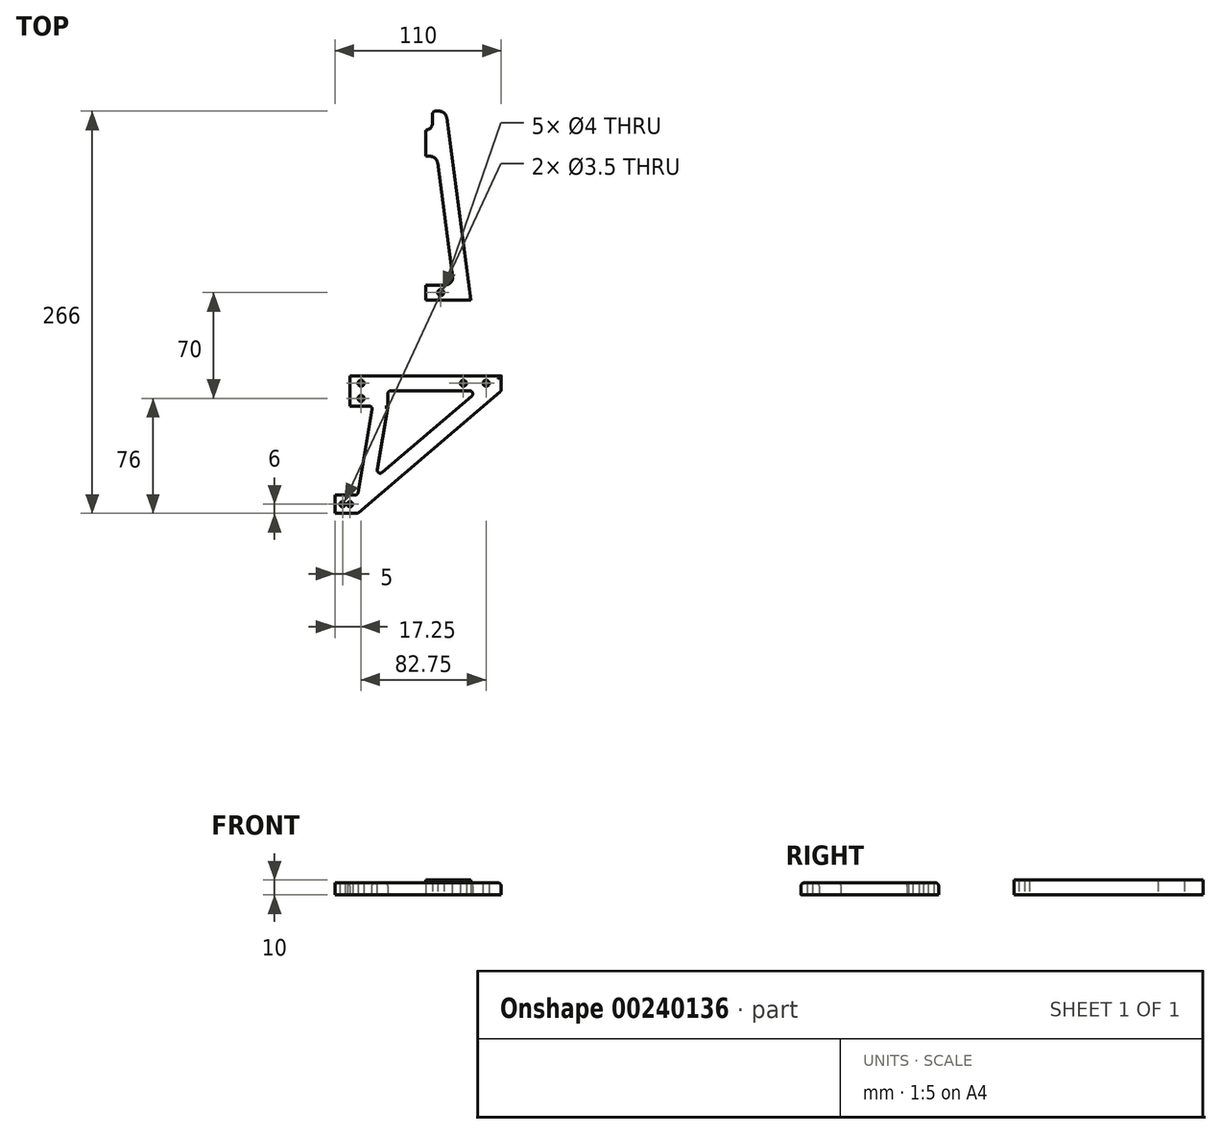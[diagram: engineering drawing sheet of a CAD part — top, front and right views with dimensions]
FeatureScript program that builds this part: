
annotation { "Feature Type Name" : "Feature", "Feature Type Description" : "" }
export const myFeature = defineFeature(function(context is Context, id is Id, definition is map)
    precondition{}
    {
        {
            var Q0;
            Q0=qCreatedBy(makeId("Top.planeOp"),FACE);
            var sketch = newSketch(context, id + "F0", { "sketchPlane" : qUnion([Q0])});
            skLineSegment(sketch, "E0.top", {"start": v(0, 75) * mm, "end": v(-30, 75) * mm});
            skPoint(sketch, "E0.middle", {"position": v(0, 0) * mm});
            skLineSegment(sketch, "E1", {"start": v(-30, 75) * mm, "end": v(-50, -75) * mm});
            skPoint(sketch, "E0.right.end.orphan", {"position": v(-50, 75) * mm});
            skPoint(sketch, "E0.left.end.orphan", {"position": v(50, 75) * mm});
            skLineSegment(sketch, "E2", {"start": v(0, 0) * mm, "end": v(0, 6) * mm});
            skLineSegment(sketch, "E3", {"start": v(-50, -75) * mm, "end": v(-40, -75) * mm});
            skLineSegment(sketch, "E4", {"start": v(-30, 75) * mm, "end": v(-20, 75) * mm});
            skLineSegment(sketch, "E5", {"start": v(0, 75) * mm, "end": v(0, 65) * mm});
            skLineSegment(sketch, "E6", {"start": v(0, 65) * mm, "end": v(-21.33, 65) * mm});
            skLineSegment(sketch, "E7", {"start": v(0, -75) * mm, "end": v(0, -65) * mm});
            skLineSegment(sketch, "E8", {"start": v(0, -65) * mm, "end": v(-38.67, -65) * mm});
            skLineSegment(sketch, "E9", {"start": v(0, 6) * mm, "end": v(-29.2, 6) * mm});
            skLineSegment(sketch, "E10", {"start": v(0, 0) * mm, "end": v(0, -6) * mm});
            skLineSegment(sketch, "E11", {"start": v(0, -6) * mm, "end": v(-30.8, -6) * mm});
            skLineSegment(sketch, "E12.trimOffspring", {"start": v(-30.8, -6) * mm, "end": v(-38.67, -65) * mm});
            skLineSegment(sketch, "E13", {"start": v(-21.33, 65) * mm, "end": v(-29.2, 6) * mm});
            skLineSegment(sketch, "E14.trimOffspring", {"start": v(0, -75) * mm, "end": v(-50, -75) * mm});
            skPoint(sketch, "E0.bottom.start.orphan", {"position": v(50, -75) * mm});
            skCircle(sketch, "E15", {"center": v(-15, 0) * mm, "radius": 2 * mm});
            skLineSegment(sketch, "E16", {"start": v(0, 65) * mm, "end": v(0, 70) * mm});
            skCircle(sketch, "E17", {"center": v(-10.41, 70) * mm, "radius": 2 * mm});
            skSolve(sketch);
        }
        {
            var Q0;
            Q0=qSketchRegion(id+"F0",true);
            extrude(context, id + "F1", {"entities" : qUnion([Q0]), "depth" : 10 * mm});
        }
        {
            var Q0;
            Q0=makeQuery(id+"F1.opExtrude","SWEPT_EDGE",EDGE,{"disambiguationData":[OSD([sQuery(id+"F0.wireOp",EDGE,"E6"),sQuery(id+"F0.wireOp",EDGE,"E13")])]});
            var Q1;
            Q1=makeQuery(id+"F1.opExtrude","SWEPT_EDGE",EDGE,{"disambiguationData":[OSD([sQuery(id+"F0.wireOp",EDGE,"E11"),sQuery(id+"F0.wireOp",EDGE,"E12.trimOffspring")])]});
            var Q2;
            Q2=makeQuery(id+"F1.opExtrude","SWEPT_EDGE",EDGE,{"disambiguationData":[OSD([sQuery(id+"F0.wireOp",EDGE,"E9"),sQuery(id+"F0.wireOp",EDGE,"E13")])]});
            var Q3;
            Q3=makeQuery(id+"F1.opExtrude","SWEPT_EDGE",EDGE,{"disambiguationData":[OSD([sQuery(id+"F0.wireOp",EDGE,"E8"),sQuery(id+"F0.wireOp",EDGE,"E12.trimOffspring")])]});
            var Q4;
            Q4=makeQuery(id+"F1.opExtrude","SWEPT_EDGE",EDGE,{"disambiguationData":[OSD([sQuery(id+"F0.wireOp",EDGE,"E1"),sQuery(id+"F0.wireOp",EDGE,"E14.trimOffspring")])]});
            fillet(context, id + "F2", {"entities" : qUnion([Q0, Q1, Q2, Q3, Q4]), "radius" : 5 * mm, "tangentPropagation" : true, "allowEdgeOverflow" : false});
        }
        {
            var Q0;
            Q0=makeQuery(id+"F1.opExtrude","SWEPT_BODY",BODY,{"disambiguationData":[OSD([sQuery(id+"F0.wireOp",EDGE,"E0.top"),sQuery(id+"F0.wireOp",EDGE,"E1"),sQuery(id+"F0.wireOp",EDGE,"E2"),sQuery(id+"F0.wireOp",EDGE,"E4"),sQuery(id+"F0.wireOp",EDGE,"E5"),sQuery(id+"F0.wireOp",EDGE,"E6"),sQuery(id+"F0.wireOp",EDGE,"E7"),sQuery(id+"F0.wireOp",EDGE,"E8"),sQuery(id+"F0.wireOp",EDGE,"E9"),sQuery(id+"F0.wireOp",EDGE,"E10"),sQuery(id+"F0.wireOp",EDGE,"E11"),sQuery(id+"F0.wireOp",EDGE,"E12.trimOffspring"),sQuery(id+"F0.wireOp",EDGE,"E13"),sQuery(id+"F0.wireOp",EDGE,"E14.trimOffspring"),sQuery(id+"F0.wireOp",EDGE,"E15"),sQuery(id+"F0.wireOp",EDGE,"E16"),sQuery(id+"F0.wireOp",EDGE,"E17")])]});
            var Q1;
            Q1=qCreatedBy(makeId("Right.planeOp"),FACE);
            mirror(context, id + "F3", {"operationType" : NewBodyOperationType.ADD, "entities" : qUnion([Q0]), "mirrorPlane" : qUnion([Q1])});
        }
        {
            var Q0;
            Q0=qCreatedBy(makeId("Top.planeOp"),FACE);
            var sketch = newSketch(context, id + "F4", { "sketchPlane" : qUnion([Q0])});
            skLineSegment(sketch, "E18", {"start": v(0, 0) * mm, "end": v(40, 0) * mm});
            skLineSegment(sketch, "E19", {"start": v(0, 75) * mm, "end": v(30, 75) * mm});
            skLineSegment(sketch, "E20", {"start": v(0, 75) * mm, "end": v(0, 85) * mm});
            skLineSegment(sketch, "E21", {"start": v(4.5, 200) * mm, "end": v(13.33, 200) * mm});
            skLineSegment(sketch, "E22", {"start": v(30, 75) * mm, "end": v(13.33, 200) * mm});
            skArc(sketch, "E23", {"start": v(0, 187.5) * mm, "mid": v(3.18, 188.82) * mm, "end": v(4.5, 192) * mm});
            skLineSegment(sketch, "E24", {"start": v(4.5, 200) * mm, "end": v(4.5, 192) * mm});
            skLineSegment(sketch, "E25", {"start": v(0, 75) * mm, "end": v(0, 80) * mm});
            skCircle(sketch, "E26", {"center": v(10, 80) * mm, "radius": 2 * mm});
            skLineSegment(sketch, "E27", {"start": v(0, 75) * mm, "end": v(10, 75) * mm});
            skLineSegment(sketch, "E28", {"start": v(10, 85) * mm, "end": v(18.67, 85) * mm});
            skLineSegment(sketch, "E29", {"start": v(18.67, 85) * mm, "end": v(10, 150) * mm});
            skLineSegment(sketch, "E30", {"start": v(10, 85) * mm, "end": v(0, 85) * mm});
            skLineSegment(sketch, "E31", {"start": v(18.67, 85) * mm, "end": v(7.31, 170.17) * mm});
            skLineSegment(sketch, "E32", {"start": v(7.31, 170.17) * mm, "end": v(0, 170.17) * mm});
            skLineSegment(sketch, "E33.trimOffspring", {"start": v(0, 170.17) * mm, "end": v(0, 187.5) * mm});
            skSolve(sketch);
        }
        {
            var Q0;
            Q0=qSketchRegion(id+"F4",true);
            extrude(context, id + "F5", {"entities" : qUnion([Q0]), "depth" : 10 * mm});
        }
        {
            var Q0;
            Q0=makeQuery(id+"F5.opExtrude","SWEPT_BODY",BODY,{"disambiguationData":[OSD([sQuery(id+"F4.wireOp",EDGE,"E19"),sQuery(id+"F4.wireOp",EDGE,"E20"),sQuery(id+"F4.wireOp",EDGE,"E21"),sQuery(id+"F4.wireOp",EDGE,"E22"),sQuery(id+"F4.wireOp",EDGE,"E23"),sQuery(id+"F4.wireOp",EDGE,"E24"),sQuery(id+"F4.wireOp",EDGE,"E25"),sQuery(id+"F4.wireOp",EDGE,"E26"),sQuery(id+"F4.wireOp",EDGE,"E27"),sQuery(id+"F4.wireOp",EDGE,"E28"),sQuery(id+"F4.wireOp",EDGE,"E30"),sQuery(id+"F4.wireOp",EDGE,"E31"),sQuery(id+"F4.wireOp",EDGE,"E32"),sQuery(id+"F4.wireOp",EDGE,"E33.trimOffspring")])]});
            var Q1;
            Q1=qCreatedBy(makeId("Right.planeOp"),FACE);
            mirror(context, id + "F6", {"entities" : qUnion([Q0]), "mirrorPlane" : qUnion([Q1])});
        }
        {
            var Q0;
            Q0=makeQuery(id+"F6.opPattern","COPY",EDGE,{"derivedFrom":makeQuery(id+"F5.opExtrude","SWEPT_EDGE",EDGE,{"disambiguationData":[OSD([sQuery(id+"F4.wireOp",EDGE,"E31"),sQuery(id+"F4.wireOp",EDGE,"E32")])]}),"instanceName":"1"});
            var Q1;
            Q1=makeQuery(id+"F5.opExtrude","SWEPT_EDGE",EDGE,{"disambiguationData":[OSD([sQuery(id+"F4.wireOp",EDGE,"E31"),sQuery(id+"F4.wireOp",EDGE,"E32")])]});
            var Q2;
            Q2=makeQuery(id+"F6.opPattern","COPY",EDGE,{"derivedFrom":makeQuery(id+"F5.opExtrude","SWEPT_EDGE",EDGE,{"disambiguationData":[OSD([sQuery(id+"F4.wireOp",EDGE,"E28"),sQuery(id+"F4.wireOp",EDGE,"E31")])]}),"instanceName":"1"});
            var Q3;
            Q3=makeQuery(id+"F5.opExtrude","SWEPT_EDGE",EDGE,{"disambiguationData":[OSD([sQuery(id+"F4.wireOp",EDGE,"E28"),sQuery(id+"F4.wireOp",EDGE,"E31")])]});
            var Q4;
            Q4=makeQuery(id+"F6.opPattern","COPY",EDGE,{"derivedFrom":makeQuery(id+"F5.opExtrude","SWEPT_EDGE",EDGE,{"disambiguationData":[OSD([sQuery(id+"F4.wireOp",EDGE,"E21"),sQuery(id+"F4.wireOp",EDGE,"E22")])]}),"instanceName":"1"});
            var Q5;
            Q5=makeQuery(id+"F5.opExtrude","SWEPT_EDGE",EDGE,{"disambiguationData":[OSD([sQuery(id+"F4.wireOp",EDGE,"E21"),sQuery(id+"F4.wireOp",EDGE,"E22")])]});
            fillet(context, id + "F7", {"entities" : qUnion([Q0, Q1, Q2, Q3, Q4, Q5]), "radius" : 5 * mm, "tangentPropagation" : true, "allowEdgeOverflow" : false});
        }
        {
            var Q0;
            Q0=makeQuery(id+"F5.opExtrude","SWEPT_EDGE",EDGE,{"disambiguationData":[OSD([sQuery(id+"F4.wireOp",EDGE,"E21"),sQuery(id+"F4.wireOp",EDGE,"E24")])]});
            var Q1;
            Q1=makeQuery(id+"F6.opPattern","COPY",EDGE,{"derivedFrom":makeQuery(id+"F5.opExtrude","SWEPT_EDGE",EDGE,{"disambiguationData":[OSD([sQuery(id+"F4.wireOp",EDGE,"E21"),sQuery(id+"F4.wireOp",EDGE,"E24")])]}),"instanceName":"1"});
            fillet(context, id + "F8", {"entities" : qUnion([Q0, Q1]), "radius" : 2 * mm, "tangentPropagation" : true, "allowEdgeOverflow" : false});
        }
        {
            var Q0;
            Q0=qCreatedBy(makeId("Top.planeOp"),FACE);
            var sketch = newSketch(context, id + "F9", { "sketchPlane" : qUnion([Q0])});
            skLineSegment(sketch, "E34", {"start": v(0, 0) * mm, "end": v(0, 6) * mm});
            skLineSegment(sketch, "E35", {"start": v(0, 6) * mm, "end": v(-6, 6) * mm});
            skLineSegment(sketch, "E36", {"start": v(-6, 6) * mm, "end": v(-6, -6) * mm});
            skLineSegment(sketch, "E37", {"start": v(-6, -6) * mm, "end": v(0, -6) * mm});
            skLineSegment(sketch, "E38", {"start": v(0, -6) * mm, "end": v(0, 0) * mm});
            skSolve(sketch);
        }
        {
            var Q0;
            Q0=qSketchRegion(id+"F9",true);
            extrude(context, id + "F10", {"entities" : qUnion([Q0]), "operationType" : NewBodyOperationType.ADD, "depth" : 25 * mm});
        }
        {
            var Q0;
            Q0=makeQuery(id+"F10.opExtrude","SWEPT_EDGE",EDGE,{"disambiguationData":[OSD([sQuery(id+"F9.wireOp",EDGE,"E36"),sQuery(id+"F9.wireOp",EDGE,"E37")])]});
            var Q1;
            Q1=makeQuery(id+"F10.opExtrude","CAP_EDGE",EDGE,{"disambiguationData":[OSD([sQuery(id+"F9.wireOp",EDGE,"E36")])],"isStart":false});
            var Q2;
            Q2=makeQuery(id+"F10.opExtrude","CAP_EDGE",EDGE,{"disambiguationData":[OSD([sQuery(id+"F9.wireOp",EDGE,"E37")])],"isStart":false});
            var Q3;
            Q3=makeQuery(id+"F10.opExtrude","SWEPT_EDGE",EDGE,{"disambiguationData":[OSD([sQuery(id+"F9.wireOp",EDGE,"E35"),sQuery(id+"F9.wireOp",EDGE,"E36")])]});
            var Q4;
            Q4=makeQuery(id+"F10.opExtrude","CAP_EDGE",EDGE,{"disambiguationData":[OSD([sQuery(id+"F9.wireOp",EDGE,"E35")])],"isStart":false});
            fillet(context, id + "F11", {"entities" : qUnion([Q0, Q1, Q2, Q3, Q4]), "radius" : 1.5 * mm, "tangentPropagation" : true, "allowEdgeOverflow" : false});
        }
        {
            var Q0;
            Q0=qCreatedBy(makeId("Right.planeOp"),FACE);
            var sketch = newSketch(context, id + "F12", { "sketchPlane" : qUnion([Q0])});
            skCircle(sketch, "E39", {"center": v(0, 20) * mm, "radius": 1.75 * mm});
            skCircle(sketch, "E40", {"center": v(0, 15) * mm, "radius": 1.75 * mm});
            skSolve(sketch);
        }
        {
            var Q0;
            Q0=qSketchRegion(id+"F12",true);
            extrude(context, id + "F13", {"entities" : qUnion([Q0]), "endBound" : BoundingType.SYMMETRIC, "depth" : 25 * mm});
        }
        {
            var Q0;
            Q0=makeQuery(id+"F13.opExtrude","SWEPT_BODY",BODY,{"disambiguationData":[OSD([sQuery(id+"F12.wireOp",EDGE,"E40")])]});
            var Q1;
            Q1=makeQuery(id+"F13.opExtrude","SWEPT_BODY",BODY,{"disambiguationData":[OSD([sQuery(id+"F12.wireOp",EDGE,"E39")])]});
            var Q2;
            Q2=makeQuery(id+"F1.opExtrude","SWEPT_BODY",BODY,{"disambiguationData":[OSD([sQuery(id+"F0.wireOp",EDGE,"E0.top"),sQuery(id+"F0.wireOp",EDGE,"E1"),sQuery(id+"F0.wireOp",EDGE,"E2"),sQuery(id+"F0.wireOp",EDGE,"E4"),sQuery(id+"F0.wireOp",EDGE,"E5"),sQuery(id+"F0.wireOp",EDGE,"E6"),sQuery(id+"F0.wireOp",EDGE,"E7"),sQuery(id+"F0.wireOp",EDGE,"E8"),sQuery(id+"F0.wireOp",EDGE,"E9"),sQuery(id+"F0.wireOp",EDGE,"E10"),sQuery(id+"F0.wireOp",EDGE,"E11"),sQuery(id+"F0.wireOp",EDGE,"E12.trimOffspring"),sQuery(id+"F0.wireOp",EDGE,"E13"),sQuery(id+"F0.wireOp",EDGE,"E14.trimOffspring"),sQuery(id+"F0.wireOp",EDGE,"E15"),sQuery(id+"F0.wireOp",EDGE,"E16"),sQuery(id+"F0.wireOp",EDGE,"E17")])]});
            booleanBodies(context, id + "F14", {"operationType" : BooleanOperationType.SUBTRACTION, "tools" : qUnion([Q0, Q1]), "targets" : qUnion([Q2])});
        }
        {
            var Q0;
            Q0=qCreatedBy(makeId("Top.planeOp"),FACE);
            var sketch = newSketch(context, id + "F15", { "sketchPlane" : qUnion([Q0])});
            skLineSegment(sketch, "E41.bottom", {"start": v(15, 65) * mm, "end": v(-15, 65) * mm});
            skLineSegment(sketch, "E41.top", {"start": v(15, 85) * mm, "end": v(-15, 85) * mm});
            skLineSegment(sketch, "E41.left", {"start": v(15, 65) * mm, "end": v(15, 85) * mm});
            skLineSegment(sketch, "E41.right", {"start": v(-15, 65) * mm, "end": v(-15, 85) * mm});
            skPoint(sketch, "E41.middle", {"position": v(0, 75) * mm});
            skLineSegment(sketch, "E42", {"start": v(0, 75) * mm, "end": v(0, 85) * mm});
            skLineSegment(sketch, "E43", {"start": v(0, 85) * mm, "end": v(0, 65) * mm});
            skLineSegment(sketch, "E44", {"start": v(0, 65) * mm, "end": v(-6, 65) * mm});
            skLineSegment(sketch, "E45", {"start": v(-6, 65) * mm, "end": v(-6, 85) * mm});
            skLineSegment(sketch, "E46", {"start": v(-6, 85) * mm, "end": v(0, 85) * mm});
            skSolve(sketch);
        }
        {
            var Q0;
            Q0=qSketchRegion(id+"F15",true);
            extrude(context, id + "F16", {"entities" : qUnion([Q0]), "depth" : 10 * mm});
        }
        {
            var Q0;
            Q0=qCreatedBy(makeId("Top.planeOp"),FACE);
            var sketch = newSketch(context, id + "F17", { "sketchPlane" : qUnion([Q0])});
            skLineSegment(sketch, "E47", {"start": v(0, 65) * mm, "end": v(0, 85) * mm});
            skLineSegment(sketch, "E48", {"start": v(0, 85) * mm, "end": v(-6, 85) * mm});
            skLineSegment(sketch, "E49", {"start": v(-6, 85) * mm, "end": v(-6, 65) * mm});
            skLineSegment(sketch, "E50", {"start": v(-6, 65) * mm, "end": v(0, 65) * mm});
            skSolve(sketch);
        }
        {
            var Q0;
            Q0=qSketchRegion(id+"F17",true);
            extrude(context, id + "F18", {"entities" : qUnion([Q0]), "depth" : 25 * mm});
        }
        {
            var Q0;
            Q0=makeQuery(id+"F16.opExtrude","SWEPT_BODY",BODY,{"disambiguationData":[OSD([sQuery(id+"F15.wireOp",EDGE,"E41.bottom"),sQuery(id+"F15.wireOp",EDGE,"E41.top"),sQuery(id+"F15.wireOp",EDGE,"E41.left"),sQuery(id+"F15.wireOp",EDGE,"E41.right"),sQuery(id+"F15.wireOp",EDGE,"E44"),sQuery(id+"F15.wireOp",EDGE,"E46")])]});
            var Q1;
            Q1=makeQuery(id+"F18.opExtrude","SWEPT_BODY",BODY,{"disambiguationData":[OSD([sQuery(id+"F17.wireOp",EDGE,"E47"),sQuery(id+"F17.wireOp",EDGE,"E48"),sQuery(id+"F17.wireOp",EDGE,"E49"),sQuery(id+"F17.wireOp",EDGE,"E50")])]});
            booleanBodies(context, id + "F19", {"operationType" : BooleanOperationType.UNION, "tools" : qUnion([Q0, Q1])});
        }
        {
            var Q0;
            Q0=makeQuery(id+"F16.opExtrude","SWEPT_BODY",BODY,{"disambiguationData":[OSD([sQuery(id+"F15.wireOp",EDGE,"E41.bottom"),sQuery(id+"F15.wireOp",EDGE,"E41.top"),sQuery(id+"F15.wireOp",EDGE,"E41.left"),sQuery(id+"F15.wireOp",EDGE,"E41.right"),sQuery(id+"F15.wireOp",EDGE,"E44"),sQuery(id+"F15.wireOp",EDGE,"E46")])]});
            transform(context, id + "F20", {"entities" : qUnion([Q0]), "transformType" : TransformType.TRANSLATION_3D, "dx" : 0 * mm, "dy" : 0 * mm, "dz" : 10 * mm, "makeCopy" : false});
        }
        {
            var Q0;
            Q0=qCreatedBy(makeId("Top.planeOp"),FACE);
            var sketch = newSketch(context, id + "F21", { "sketchPlane" : qUnion([Q0])});
            skCircle(sketch, "E51", {"center": v(-10, 80) * mm, "radius": 2 * mm});
            skCircle(sketch, "E52", {"center": v(10, 80) * mm, "radius": 2 * mm});
            skCircle(sketch, "E53", {"center": v(-10.4, 70) * mm, "radius": 2 * mm});
            skCircle(sketch, "E54", {"center": v(10.4, 70) * mm, "radius": 2 * mm});
            skSolve(sketch);
        }
        {
            var Q0;
            Q0=qSketchRegion(id+"F21",true);
            extrude(context, id + "F22", {"entities" : qUnion([Q0]), "depth" : 30 * mm});
        }
        {
            var Q0;
            Q0=makeQuery(id+"F22.opExtrude","SWEPT_BODY",BODY,{"disambiguationData":[OSD([sQuery(id+"F21.wireOp",EDGE,"E54")])]});
            var Q1;
            Q1=makeQuery(id+"F22.opExtrude","SWEPT_BODY",BODY,{"disambiguationData":[OSD([sQuery(id+"F21.wireOp",EDGE,"E53")])]});
            var Q2;
            Q2=makeQuery(id+"F22.opExtrude","SWEPT_BODY",BODY,{"disambiguationData":[OSD([sQuery(id+"F21.wireOp",EDGE,"E52")])]});
            var Q3;
            Q3=makeQuery(id+"F22.opExtrude","SWEPT_BODY",BODY,{"disambiguationData":[OSD([sQuery(id+"F21.wireOp",EDGE,"E51")])]});
            var Q4;
            Q4=makeQuery(id+"F16.opExtrude","SWEPT_BODY",BODY,{"disambiguationData":[OSD([sQuery(id+"F15.wireOp",EDGE,"E41.bottom"),sQuery(id+"F15.wireOp",EDGE,"E41.top"),sQuery(id+"F15.wireOp",EDGE,"E41.left"),sQuery(id+"F15.wireOp",EDGE,"E41.right"),sQuery(id+"F15.wireOp",EDGE,"E44"),sQuery(id+"F15.wireOp",EDGE,"E46")])]});
            booleanBodies(context, id + "F23", {"operationType" : BooleanOperationType.SUBTRACTION, "tools" : qUnion([Q0, Q1, Q2, Q3]), "targets" : qUnion([Q4])});
        }
        {
            var Q0;
            Q0=qCreatedBy(makeId("Right.planeOp"),FACE);
            var sketch = newSketch(context, id + "F24", { "sketchPlane" : qUnion([Q0])});
            skCircle(sketch, "E55", {"center": v(80, 27.23) * mm, "radius": 2 * mm});
            skCircle(sketch, "E56", {"center": v(70, 27.23) * mm, "radius": 2 * mm});
            skSolve(sketch);
        }
        {
            var Q0;
            Q0=qSketchRegion(id+"F24",true);
            extrude(context, id + "F25", {"entities" : qUnion([Q0]), "endBound" : BoundingType.SYMMETRIC, "depth" : 25 * mm});
        }
        {
            var Q0;
            Q0=makeQuery(id+"F25.opExtrude","SWEPT_BODY",BODY,{"disambiguationData":[OSD([sQuery(id+"F24.wireOp",EDGE,"E56")])]});
            var Q1;
            Q1=makeQuery(id+"F25.opExtrude","SWEPT_BODY",BODY,{"disambiguationData":[OSD([sQuery(id+"F24.wireOp",EDGE,"E55")])]});
            var Q2;
            Q2=makeQuery(id+"F16.opExtrude","SWEPT_BODY",BODY,{"disambiguationData":[OSD([sQuery(id+"F15.wireOp",EDGE,"E41.bottom"),sQuery(id+"F15.wireOp",EDGE,"E41.top"),sQuery(id+"F15.wireOp",EDGE,"E41.left"),sQuery(id+"F15.wireOp",EDGE,"E41.right"),sQuery(id+"F15.wireOp",EDGE,"E44"),sQuery(id+"F15.wireOp",EDGE,"E46")])]});
            booleanBodies(context, id + "F26", {"operationType" : BooleanOperationType.SUBTRACTION, "tools" : qUnion([Q0, Q1]), "targets" : qUnion([Q2])});
        }
        {
            var Q0;
            Q0=makeQuery(id+"F18.opExtrude","SWEPT_EDGE",EDGE,{"disambiguationData":[OSD([sQuery(id+"F17.wireOp",EDGE,"E49"),sQuery(id+"F17.wireOp",EDGE,"E50")])]});
            var Q1;
            Q1=makeQuery(id+"F18.opExtrude","CAP_EDGE",EDGE,{"disambiguationData":[OSD([sQuery(id+"F17.wireOp",EDGE,"E50")])],"isStart":false});
            var Q2;
            {var subQ0=sQuery(id+"F15.wireOp",EDGE,"E44");var subQ1=sQuery(id+"F15.wireOp",EDGE,"E41.bottom");var subQ2=sQuery(id+"F15.wireOp",EDGE,"E41.right");Q2=makeQuery(id+"F19.opBoolean","SPLIT",EDGE,{"disambiguationData":[TD([makeQuery(id+"F16.opExtrude","SWEPT_FACE",FACE,{"disambiguationData":[OSD([subQ2])]})])],"derivedFrom":makeQuery(id+"F16.opExtrude","CAP_EDGE",EDGE,{"disambiguationData":[OSD([subQ1,subQ0])],"isStart":false})});}
            var Q3;
            Q3=makeQuery(id+"F16.opExtrude","SWEPT_EDGE",EDGE,{"disambiguationData":[OSD([sQuery(id+"F15.wireOp",EDGE,"E41.bottom"),sQuery(id+"F15.wireOp",EDGE,"E41.right")])]});
            var Q4;
            {var subQ0=sQuery(id+"F15.wireOp",EDGE,"E41.left");var subQ1=sQuery(id+"F15.wireOp",EDGE,"E44");var subQ2=sQuery(id+"F15.wireOp",EDGE,"E41.bottom");Q4=makeQuery(id+"F19.opBoolean","SPLIT",EDGE,{"disambiguationData":[TD([makeQuery(id+"F16.opExtrude","SWEPT_FACE",FACE,{"disambiguationData":[OSD([subQ0])]})])],"derivedFrom":makeQuery(id+"F16.opExtrude","CAP_EDGE",EDGE,{"disambiguationData":[OSD([subQ2,subQ1])],"isStart":false})});}
            var Q5;
            Q5=makeQuery(id+"F16.opExtrude","SWEPT_EDGE",EDGE,{"disambiguationData":[OSD([sQuery(id+"F15.wireOp",EDGE,"E41.bottom"),sQuery(id+"F15.wireOp",EDGE,"E41.left")])]});
            var Q6;
            Q6=makeQuery(id+"F16.opExtrude","CAP_EDGE",EDGE,{"disambiguationData":[OSD([sQuery(id+"F15.wireOp",EDGE,"E41.left")])],"isStart":false});
            var Q7;
            Q7=makeQuery(id+"F16.opExtrude","CAP_EDGE",EDGE,{"disambiguationData":[OSD([sQuery(id+"F15.wireOp",EDGE,"E41.right")])],"isStart":false});
            var Q8;
            Q8=makeQuery(id+"F18.opExtrude","CAP_EDGE",EDGE,{"disambiguationData":[OSD([sQuery(id+"F17.wireOp",EDGE,"E49")])],"isStart":false});
            var Q9;
            {var subQ0=sQuery(id+"F15.wireOp",EDGE,"E41.right");var subQ1=sQuery(id+"F15.wireOp",EDGE,"E46");var subQ2=sQuery(id+"F15.wireOp",EDGE,"E41.top");Q9=makeQuery(id+"F19.opBoolean","SPLIT",EDGE,{"disambiguationData":[TD([makeQuery(id+"F16.opExtrude","SWEPT_FACE",FACE,{"disambiguationData":[OSD([subQ0])]})])],"derivedFrom":makeQuery(id+"F16.opExtrude","CAP_EDGE",EDGE,{"disambiguationData":[OSD([subQ2,subQ1])],"isStart":false})});}
            var Q10;
            Q10=makeQuery(id+"F16.opExtrude","SWEPT_EDGE",EDGE,{"disambiguationData":[OSD([sQuery(id+"F15.wireOp",EDGE,"E41.top"),sQuery(id+"F15.wireOp",EDGE,"E41.right")])]});
            var Q11;
            Q11=makeQuery(id+"F18.opExtrude","SWEPT_EDGE",EDGE,{"disambiguationData":[OSD([sQuery(id+"F17.wireOp",EDGE,"E48"),sQuery(id+"F17.wireOp",EDGE,"E49")])]});
            var Q12;
            Q12=makeQuery(id+"F18.opExtrude","CAP_EDGE",EDGE,{"disambiguationData":[OSD([sQuery(id+"F17.wireOp",EDGE,"E48")])],"isStart":false});
            var Q13;
            {var subQ0=sQuery(id+"F15.wireOp",EDGE,"E41.left");var subQ1=sQuery(id+"F15.wireOp",EDGE,"E46");var subQ2=sQuery(id+"F15.wireOp",EDGE,"E41.top");Q13=makeQuery(id+"F19.opBoolean","SPLIT",EDGE,{"disambiguationData":[TD([makeQuery(id+"F16.opExtrude","SWEPT_FACE",FACE,{"disambiguationData":[OSD([subQ0])]})])],"derivedFrom":makeQuery(id+"F16.opExtrude","CAP_EDGE",EDGE,{"disambiguationData":[OSD([subQ2,subQ1])],"isStart":false})});}
            var Q14;
            Q14=makeQuery(id+"F16.opExtrude","SWEPT_EDGE",EDGE,{"disambiguationData":[OSD([sQuery(id+"F15.wireOp",EDGE,"E41.top"),sQuery(id+"F15.wireOp",EDGE,"E41.left")])]});
            fillet(context, id + "F27", {"entities" : qUnion([Q0, Q1, Q2, Q3, Q4, Q5, Q6, Q7, Q8, Q9, Q10, Q11, Q12, Q13, Q14]), "radius" : 2 * mm, "tangentPropagation" : true, "allowEdgeOverflow" : false});
        }
        {
            var Q0;
            Q0=qCreatedBy(makeId("Right.planeOp"),FACE);
            var sketch = newSketch(context, id + "F28", { "sketchPlane" : qUnion([Q0])});
            skLineSegment(sketch, "E57", {"start": v(0, 0) * mm, "end": v(0, 10) * mm});
            skLineSegment(sketch, "E58", {"start": v(0, 10) * mm, "end": v(6, 10) * mm});
            skLineSegment(sketch, "E59", {"start": v(6, 10) * mm, "end": v(6, 25) * mm});
            skLineSegment(sketch, "E60", {"start": v(-6, 25) * mm, "end": v(-6, 10) * mm});
            skLineSegment(sketch, "E61", {"start": v(-6, 10) * mm, "end": v(0, 10) * mm});
            skLineSegment(sketch, "E62", {"start": v(75, 10) * mm, "end": v(75, 20) * mm});
            skLineSegment(sketch, "E63", {"start": v(75, 20) * mm, "end": v(85, 20) * mm});
            skLineSegment(sketch, "E64", {"start": v(85, 20) * mm, "end": v(85, 35) * mm});
            skLineSegment(sketch, "E65", {"start": v(65, 35) * mm, "end": v(65, 20) * mm});
            skLineSegment(sketch, "E66", {"start": v(65, 20) * mm, "end": v(75, 20) * mm});
            skLineSegment(sketch, "E67", {"start": v(-6, 10) * mm, "end": v(-6, 25) * mm});
            skLineSegment(sketch, "E68", {"start": v(75, 120) * mm, "end": v(85, 120) * mm});
            skLineSegment(sketch, "E69", {"start": v(85, 35) * mm, "end": v(85, 120) * mm});
            skLineSegment(sketch, "E70", {"start": v(85, 120) * mm, "end": v(75, 120) * mm});
            skLineSegment(sketch, "E71", {"start": v(6, 25) * mm, "end": v(65, 35) * mm});
            skLineSegment(sketch, "E72", {"start": v(-6, 25) * mm, "end": v(75, 120) * mm});
            skLineSegment(sketch, "E73", {"start": v(23.92, 44.68) * mm, "end": v(75, 104.59) * mm});
            skLineSegment(sketch, "E74", {"start": v(23.92, 44.68) * mm, "end": v(17.44, 37.08) * mm});
            skLineSegment(sketch, "E75", {"start": v(75, 45) * mm, "end": v(64.16, 45) * mm});
            skLineSegment(sketch, "E76", {"start": v(51.92, 42.93) * mm, "end": v(17.44, 37.08) * mm});
            skLineSegment(sketch, "E77", {"start": v(51.92, 42.93) * mm, "end": v(64.16, 45) * mm});
            skPoint(sketch, "E78.orphan", {"position": v(75, 35) * mm});
            skPoint(sketch, "E79.start.orphan", {"position": v(75, 110) * mm});
            skLineSegment(sketch, "E80", {"start": v(75, 104.59) * mm, "end": v(75, 45) * mm});
            skCircle(sketch, "E81", {"center": v(80, 110) * mm, "radius": 2 * mm});
            skCircle(sketch, "E82", {"center": v(80, 95) * mm, "radius": 2 * mm});
            skPoint(sketch, "E83.end.orphan", {"position": v(80, 120) * mm});
            skSolve(sketch);
        }
        {
            var Q0;
            Q0=qSketchRegion(id+"F28",true);
            extrude(context, id + "F29", {"entities" : qUnion([Q0]), "depth" : 8 * mm});
        }
        {
            var Q0;
            Q0=makeQuery(id+"F29.opExtrude","SWEPT_EDGE",EDGE,{"disambiguationData":[OSD([sQuery(id+"F28.wireOp",EDGE,"E73"),sQuery(id+"F28.wireOp",EDGE,"E80")])]});
            var Q1;
            Q1=makeQuery(id+"F29.opExtrude","SWEPT_EDGE",EDGE,{"disambiguationData":[OSD([sQuery(id+"F28.wireOp",EDGE,"E75"),sQuery(id+"F28.wireOp",EDGE,"E80")])]});
            var Q2;
            Q2=makeQuery(id+"F29.opExtrude","SWEPT_EDGE",EDGE,{"disambiguationData":[OSD([sQuery(id+"F28.wireOp",EDGE,"E74"),sQuery(id+"F28.wireOp",EDGE,"E76")])]});
            var Q3;
            Q3=makeQuery(id+"F29.opExtrude","SWEPT_EDGE",EDGE,{"disambiguationData":[OSD([sQuery(id+"F28.wireOp",EDGE,"E65"),sQuery(id+"F28.wireOp",EDGE,"E71")])]});
            var Q4;
            Q4=makeQuery(id+"F29.opExtrude","SWEPT_EDGE",EDGE,{"disambiguationData":[OSD([sQuery(id+"F28.wireOp",EDGE,"E59"),sQuery(id+"F28.wireOp",EDGE,"E71")])]});
            var Q5;
            Q5=makeQuery(id+"F29.opExtrude","SWEPT_EDGE",EDGE,{"disambiguationData":[OSD([sQuery(id+"F28.wireOp",EDGE,"E67"),sQuery(id+"F28.wireOp",EDGE,"E72")])]});
            fillet(context, id + "F30", {"entities" : qUnion([Q0, Q1, Q2, Q3, Q4, Q5]), "radius" : 2 * mm, "tangentPropagation" : true, "allowEdgeOverflow" : false});
        }
        {
            var Q0;
            Q0=makeQuery(id+"F29.opExtrude","CAP_EDGE",EDGE,{"disambiguationData":[OSD([sQuery(id+"F28.wireOp",EDGE,"E73"),sQuery(id+"F28.wireOp",EDGE,"E74")])],"isStart":false});
            var Q1;
            Q1=makeQuery(id+"F29.opExtrude","CAP_EDGE",EDGE,{"disambiguationData":[OSD([sQuery(id+"F28.wireOp",EDGE,"E72")])],"isStart":false});
            var Q2;
            Q2=makeQuery(id+"F29.opExtrude","CAP_EDGE",EDGE,{"disambiguationData":[OSD([sQuery(id+"F28.wireOp",EDGE,"E71")])],"isStart":false});
            var Q3;
            Q3=makeQuery(id+"F29.opExtrude","CAP_EDGE",EDGE,{"disambiguationData":[OSD([sQuery(id+"F28.wireOp",EDGE,"E64"),sQuery(id+"F28.wireOp",EDGE,"E69")])],"isStart":false});
            fillet(context, id + "F31", {"entities" : qUnion([Q0, Q1, Q2, Q3]), "radius" : 2 * mm, "tangentPropagation" : true, "allowEdgeOverflow" : false});
        }
        {
            var Q0;
            Q0=qCreatedBy(makeId("Right.planeOp"),FACE);
            var sketch = newSketch(context, id + "F32", { "sketchPlane" : qUnion([Q0])});
            skCircle(sketch, "E84", {"center": v(0, 20) * mm, "radius": 1.75 * mm});
            skCircle(sketch, "E85", {"center": v(0, 15) * mm, "radius": 1.75 * mm});
            skCircle(sketch, "E86", {"center": v(70, 27.25) * mm, "radius": 2 * mm});
            skCircle(sketch, "E87", {"center": v(80, 27.25) * mm, "radius": 2 * mm});
            skSolve(sketch);
        }
        {
            var Q0;
            Q0=qSketchRegion(id+"F32",true);
            extrude(context, id + "F33", {"entities" : qUnion([Q0]), "depth" : 25 * mm});
        }
        {
            var Q0;
            Q0=makeQuery(id+"F33.opExtrude","SWEPT_BODY",BODY,{"disambiguationData":[OSD([sQuery(id+"F32.wireOp",EDGE,"E87")])]});
            var Q1;
            Q1=makeQuery(id+"F33.opExtrude","SWEPT_BODY",BODY,{"disambiguationData":[OSD([sQuery(id+"F32.wireOp",EDGE,"E86")])]});
            var Q2;
            Q2=makeQuery(id+"F33.opExtrude","SWEPT_BODY",BODY,{"disambiguationData":[OSD([sQuery(id+"F32.wireOp",EDGE,"E85")])]});
            var Q3;
            Q3=makeQuery(id+"F33.opExtrude","SWEPT_BODY",BODY,{"disambiguationData":[OSD([sQuery(id+"F32.wireOp",EDGE,"E84")])]});
            var Q4;
            Q4=makeQuery(id+"F29.opExtrude","SWEPT_BODY",BODY,{"disambiguationData":[OSD([sQuery(id+"F28.wireOp",EDGE,"E59"),sQuery(id+"F28.wireOp",EDGE,"E61"),sQuery(id+"F28.wireOp",EDGE,"E58"),sQuery(id+"F28.wireOp",EDGE,"E63"),sQuery(id+"F28.wireOp",EDGE,"E64"),sQuery(id+"F28.wireOp",EDGE,"E65"),sQuery(id+"F28.wireOp",EDGE,"E66"),sQuery(id+"F28.wireOp",EDGE,"E67"),sQuery(id+"F28.wireOp",EDGE,"E69"),sQuery(id+"F28.wireOp",EDGE,"E70"),sQuery(id+"F28.wireOp",EDGE,"E71"),sQuery(id+"F28.wireOp",EDGE,"E72"),sQuery(id+"F28.wireOp",EDGE,"E73"),sQuery(id+"F28.wireOp",EDGE,"E74"),sQuery(id+"F28.wireOp",EDGE,"E75"),sQuery(id+"F28.wireOp",EDGE,"E76"),sQuery(id+"F28.wireOp",EDGE,"E77"),sQuery(id+"F28.wireOp",EDGE,"E80"),sQuery(id+"F28.wireOp",EDGE,"E81"),sQuery(id+"F28.wireOp",EDGE,"E82")])]});
            booleanBodies(context, id + "F34", {"operationType" : BooleanOperationType.SUBTRACTION, "tools" : qUnion([Q0, Q1, Q2, Q3]), "targets" : qUnion([Q4])});
        }
        {
            var Q0;
            Q0=makeQuery(id+"F16.opExtrude","SWEPT_BODY",BODY,{"disambiguationData":[OSD([sQuery(id+"F15.wireOp",EDGE,"E41.bottom"),sQuery(id+"F15.wireOp",EDGE,"E41.top"),sQuery(id+"F15.wireOp",EDGE,"E41.left"),sQuery(id+"F15.wireOp",EDGE,"E41.right"),sQuery(id+"F15.wireOp",EDGE,"E44"),sQuery(id+"F15.wireOp",EDGE,"E46")])]});
            var Q1;
            Q1=makeQuery(id+"F6.opPattern","COPY",BODY,{"derivedFrom":makeQuery(id+"F5.opExtrude","SWEPT_BODY",BODY,{"disambiguationData":[OSD([sQuery(id+"F4.wireOp",EDGE,"E19"),sQuery(id+"F4.wireOp",EDGE,"E20"),sQuery(id+"F4.wireOp",EDGE,"E21"),sQuery(id+"F4.wireOp",EDGE,"E22"),sQuery(id+"F4.wireOp",EDGE,"E23"),sQuery(id+"F4.wireOp",EDGE,"E24"),sQuery(id+"F4.wireOp",EDGE,"E25"),sQuery(id+"F4.wireOp",EDGE,"E26"),sQuery(id+"F4.wireOp",EDGE,"E27"),sQuery(id+"F4.wireOp",EDGE,"E28"),sQuery(id+"F4.wireOp",EDGE,"E30"),sQuery(id+"F4.wireOp",EDGE,"E31"),sQuery(id+"F4.wireOp",EDGE,"E32"),sQuery(id+"F4.wireOp",EDGE,"E33.trimOffspring")])]}),"instanceName":"1"});
            var Q2;
            Q2=makeQuery(id+"F1.opExtrude","SWEPT_BODY",BODY,{"disambiguationData":[OSD([sQuery(id+"F0.wireOp",EDGE,"E0.top"),sQuery(id+"F0.wireOp",EDGE,"E1"),sQuery(id+"F0.wireOp",EDGE,"E2"),sQuery(id+"F0.wireOp",EDGE,"E4"),sQuery(id+"F0.wireOp",EDGE,"E5"),sQuery(id+"F0.wireOp",EDGE,"E6"),sQuery(id+"F0.wireOp",EDGE,"E7"),sQuery(id+"F0.wireOp",EDGE,"E8"),sQuery(id+"F0.wireOp",EDGE,"E9"),sQuery(id+"F0.wireOp",EDGE,"E10"),sQuery(id+"F0.wireOp",EDGE,"E11"),sQuery(id+"F0.wireOp",EDGE,"E12.trimOffspring"),sQuery(id+"F0.wireOp",EDGE,"E13"),sQuery(id+"F0.wireOp",EDGE,"E14.trimOffspring"),sQuery(id+"F0.wireOp",EDGE,"E15"),sQuery(id+"F0.wireOp",EDGE,"E16"),sQuery(id+"F0.wireOp",EDGE,"E17")])]});
            deleteBodies(context, id + "F35", {"entities" : qUnion([Q0, Q1, Q2])});
        }
        {
            var Q0;
            Q0=qCreatedBy(makeId("Right.planeOp"),FACE);
            var sketch = newSketch(context, id + "F36", { "sketchPlane" : qUnion([Q0])});
            skLineSegment(sketch, "E88", {"start": v(0, 0) * mm, "end": v(-78.77, 0) * mm});
            skSolve(sketch);
        }
        {
            var Q0;
            Q0=makeQuery(id+"F29.opExtrude","SWEPT_BODY",BODY,{"disambiguationData":[OSD([sQuery(id+"F28.wireOp",EDGE,"E59"),sQuery(id+"F28.wireOp",EDGE,"E61"),sQuery(id+"F28.wireOp",EDGE,"E58"),sQuery(id+"F28.wireOp",EDGE,"E63"),sQuery(id+"F28.wireOp",EDGE,"E64"),sQuery(id+"F28.wireOp",EDGE,"E65"),sQuery(id+"F28.wireOp",EDGE,"E66"),sQuery(id+"F28.wireOp",EDGE,"E67"),sQuery(id+"F28.wireOp",EDGE,"E69"),sQuery(id+"F28.wireOp",EDGE,"E70"),sQuery(id+"F28.wireOp",EDGE,"E71"),sQuery(id+"F28.wireOp",EDGE,"E72"),sQuery(id+"F28.wireOp",EDGE,"E73"),sQuery(id+"F28.wireOp",EDGE,"E74"),sQuery(id+"F28.wireOp",EDGE,"E75"),sQuery(id+"F28.wireOp",EDGE,"E76"),sQuery(id+"F28.wireOp",EDGE,"E77"),sQuery(id+"F28.wireOp",EDGE,"E80"),sQuery(id+"F28.wireOp",EDGE,"E81"),sQuery(id+"F28.wireOp",EDGE,"E82")])]});
            var Q1;
            Q1=sQuery(id+"F36.wireOp",EDGE,"E88");
            transform(context, id + "F37", {"entities" : qUnion([Q0]), "transformType" : TransformType.ROTATION, "transformAxis" : qUnion([Q1]), "angle" : 90 * degree, "makeCopy" : false});
        }
        {
            var Q0;
            Q0=makeQuery(id+"F29.opExtrude","SWEPT_BODY",BODY,{"disambiguationData":[OSD([sQuery(id+"F28.wireOp",EDGE,"E59"),sQuery(id+"F28.wireOp",EDGE,"E61"),sQuery(id+"F28.wireOp",EDGE,"E58"),sQuery(id+"F28.wireOp",EDGE,"E63"),sQuery(id+"F28.wireOp",EDGE,"E64"),sQuery(id+"F28.wireOp",EDGE,"E65"),sQuery(id+"F28.wireOp",EDGE,"E66"),sQuery(id+"F28.wireOp",EDGE,"E67"),sQuery(id+"F28.wireOp",EDGE,"E69"),sQuery(id+"F28.wireOp",EDGE,"E70"),sQuery(id+"F28.wireOp",EDGE,"E71"),sQuery(id+"F28.wireOp",EDGE,"E72"),sQuery(id+"F28.wireOp",EDGE,"E73"),sQuery(id+"F28.wireOp",EDGE,"E74"),sQuery(id+"F28.wireOp",EDGE,"E75"),sQuery(id+"F28.wireOp",EDGE,"E76"),sQuery(id+"F28.wireOp",EDGE,"E77"),sQuery(id+"F28.wireOp",EDGE,"E80"),sQuery(id+"F28.wireOp",EDGE,"E81"),sQuery(id+"F28.wireOp",EDGE,"E82")])]});
            transform(context, id + "F38", {"entities" : qUnion([Q0]), "transformType" : TransformType.TRANSLATION_3D, "dx" : 120 * mm, "dy" : -60 * mm, "dz" : 0 * mm, "makeCopy" : false});
        }
        {
            var Q0;
            Q0=makeQuery(id+"F29.opExtrude","SWEPT_BODY",BODY,{"disambiguationData":[OSD([sQuery(id+"F28.wireOp",EDGE,"E59"),sQuery(id+"F28.wireOp",EDGE,"E61"),sQuery(id+"F28.wireOp",EDGE,"E58"),sQuery(id+"F28.wireOp",EDGE,"E63"),sQuery(id+"F28.wireOp",EDGE,"E64"),sQuery(id+"F28.wireOp",EDGE,"E65"),sQuery(id+"F28.wireOp",EDGE,"E66"),sQuery(id+"F28.wireOp",EDGE,"E67"),sQuery(id+"F28.wireOp",EDGE,"E69"),sQuery(id+"F28.wireOp",EDGE,"E70"),sQuery(id+"F28.wireOp",EDGE,"E71"),sQuery(id+"F28.wireOp",EDGE,"E72"),sQuery(id+"F28.wireOp",EDGE,"E73"),sQuery(id+"F28.wireOp",EDGE,"E74"),sQuery(id+"F28.wireOp",EDGE,"E75"),sQuery(id+"F28.wireOp",EDGE,"E76"),sQuery(id+"F28.wireOp",EDGE,"E77"),sQuery(id+"F28.wireOp",EDGE,"E80"),sQuery(id+"F28.wireOp",EDGE,"E81"),sQuery(id+"F28.wireOp",EDGE,"E82")])]});
            var Q1;
            Q1=qCreatedBy(makeId("Right.planeOp"),FACE);
            mirror(context, id + "F39", {"entities" : qUnion([Q0]), "mirrorPlane" : qUnion([Q1])});
        }
        {
            var Q0;
            Q0=qCreatedBy(makeId("Top.planeOp"),FACE);
            var sketch = newSketch(context, id + "F40", { "sketchPlane" : qUnion([Q0])});
            skLineSegment(sketch, "E89", {"start": v(30, 25) * mm, "end": v(30, 15) * mm});
            skLineSegment(sketch, "E90", {"start": v(30, 15) * mm, "end": v(-30, 15) * mm});
            skLineSegment(sketch, "E91", {"start": v(-30, 15) * mm, "end": v(-30, 25) * mm});
            skLineSegment(sketch, "E92", {"start": v(-30, 25) * mm, "end": v(30, 25) * mm});
            skCircle(sketch, "E93", {"center": v(-25, 20) * mm, "radius": 2 * mm});
            skCircle(sketch, "E94", {"center": v(-10, 20) * mm, "radius": 2 * mm});
            skCircle(sketch, "E95", {"center": v(10, 20) * mm, "radius": 2 * mm});
            skCircle(sketch, "E96", {"center": v(25, 20) * mm, "radius": 2 * mm});
            skPoint(sketch, "E97.end.orphan", {"position": v(-30, 20) * mm});
            skSolve(sketch);
        }
        {
            var Q0;
            Q0=qSketchRegion(id+"F40",true);
            extrude(context, id + "F41", {"entities" : qUnion([Q0]), "depth" : 8 * mm});
        }
        {
            var Q0;
            Q0=makeQuery(id+"F41.opExtrude","SWEPT_BODY",BODY,{"disambiguationData":[OSD([sQuery(id+"F40.wireOp",EDGE,"E89"),sQuery(id+"F40.wireOp",EDGE,"E90"),sQuery(id+"F40.wireOp",EDGE,"E91"),sQuery(id+"F40.wireOp",EDGE,"E92"),sQuery(id+"F40.wireOp",EDGE,"E93"),sQuery(id+"F40.wireOp",EDGE,"E94"),sQuery(id+"F40.wireOp",EDGE,"E95"),sQuery(id+"F40.wireOp",EDGE,"E96")])]});
            transform(context, id + "F42", {"entities" : qUnion([Q0]), "transformType" : TransformType.TRANSLATION_3D, "dx" : 0 * mm, "dy" : 0 * mm, "dz" : 8 * mm, "makeCopy" : false});
        }
        {
            var Q0;
            Q0=makeQuery(id+"F41.opExtrude","CAP_EDGE",EDGE,{"disambiguationData":[OSD([sQuery(id+"F40.wireOp",EDGE,"E90")])],"isStart":false});
            var Q1;
            Q1=makeQuery(id+"F41.opExtrude","SWEPT_EDGE",EDGE,{"disambiguationData":[OSD([sQuery(id+"F40.wireOp",EDGE,"E89"),sQuery(id+"F40.wireOp",EDGE,"E90")])]});
            var Q2;
            Q2=makeQuery(id+"F41.opExtrude","SWEPT_EDGE",EDGE,{"disambiguationData":[OSD([sQuery(id+"F40.wireOp",EDGE,"E89"),sQuery(id+"F40.wireOp",EDGE,"E92")])]});
            var Q3;
            Q3=makeQuery(id+"F41.opExtrude","CAP_EDGE",EDGE,{"disambiguationData":[OSD([sQuery(id+"F40.wireOp",EDGE,"E89")])],"isStart":false});
            var Q4;
            Q4=makeQuery(id+"F41.opExtrude","CAP_EDGE",EDGE,{"disambiguationData":[OSD([sQuery(id+"F40.wireOp",EDGE,"E91")])],"isStart":false});
            var Q5;
            Q5=makeQuery(id+"F41.opExtrude","SWEPT_EDGE",EDGE,{"disambiguationData":[OSD([sQuery(id+"F40.wireOp",EDGE,"E90"),sQuery(id+"F40.wireOp",EDGE,"E91")])]});
            var Q6;
            Q6=makeQuery(id+"F41.opExtrude","SWEPT_EDGE",EDGE,{"disambiguationData":[OSD([sQuery(id+"F40.wireOp",EDGE,"E91"),sQuery(id+"F40.wireOp",EDGE,"E92")])]});
            var Q7;
            Q7=makeQuery(id+"F41.opExtrude","CAP_EDGE",EDGE,{"disambiguationData":[OSD([sQuery(id+"F40.wireOp",EDGE,"E92")])],"isStart":false});
            fillet(context, id + "F43", {"entities" : qUnion([Q0, Q1, Q2, Q3, Q4, Q5, Q6, Q7]), "radius" : 1.5 * mm, "tangentPropagation" : true, "allowEdgeOverflow" : false});
        }
        {
            var Q0;
            Q0=makeQuery(id+"F29.opExtrude","SWEPT_BODY",BODY,{"disambiguationData":[OSD([sQuery(id+"F28.wireOp",EDGE,"E59"),sQuery(id+"F28.wireOp",EDGE,"E61"),sQuery(id+"F28.wireOp",EDGE,"E58"),sQuery(id+"F28.wireOp",EDGE,"E63"),sQuery(id+"F28.wireOp",EDGE,"E64"),sQuery(id+"F28.wireOp",EDGE,"E65"),sQuery(id+"F28.wireOp",EDGE,"E66"),sQuery(id+"F28.wireOp",EDGE,"E67"),sQuery(id+"F28.wireOp",EDGE,"E69"),sQuery(id+"F28.wireOp",EDGE,"E70"),sQuery(id+"F28.wireOp",EDGE,"E71"),sQuery(id+"F28.wireOp",EDGE,"E72"),sQuery(id+"F28.wireOp",EDGE,"E73"),sQuery(id+"F28.wireOp",EDGE,"E74"),sQuery(id+"F28.wireOp",EDGE,"E75"),sQuery(id+"F28.wireOp",EDGE,"E76"),sQuery(id+"F28.wireOp",EDGE,"E77"),sQuery(id+"F28.wireOp",EDGE,"E80"),sQuery(id+"F28.wireOp",EDGE,"E81"),sQuery(id+"F28.wireOp",EDGE,"E82")])]});
            var Q1;
            Q1=makeQuery(id+"F41.opExtrude","SWEPT_BODY",BODY,{"disambiguationData":[OSD([sQuery(id+"F40.wireOp",EDGE,"E89"),sQuery(id+"F40.wireOp",EDGE,"E90"),sQuery(id+"F40.wireOp",EDGE,"E91"),sQuery(id+"F40.wireOp",EDGE,"E92"),sQuery(id+"F40.wireOp",EDGE,"E93"),sQuery(id+"F40.wireOp",EDGE,"E94"),sQuery(id+"F40.wireOp",EDGE,"E95"),sQuery(id+"F40.wireOp",EDGE,"E96")])]});
            deleteBodies(context, id + "F44", {"entities" : qUnion([Q0, Q1])});
        }
        {
            var Q0;
            Q0=makeQuery(id+"F39.opPattern","COPY",BODY,{"derivedFrom":makeQuery(id+"F29.opExtrude","SWEPT_BODY",BODY,{"disambiguationData":[OSD([sQuery(id+"F28.wireOp",EDGE,"E59"),sQuery(id+"F28.wireOp",EDGE,"E61"),sQuery(id+"F28.wireOp",EDGE,"E58"),sQuery(id+"F28.wireOp",EDGE,"E63"),sQuery(id+"F28.wireOp",EDGE,"E64"),sQuery(id+"F28.wireOp",EDGE,"E65"),sQuery(id+"F28.wireOp",EDGE,"E66"),sQuery(id+"F28.wireOp",EDGE,"E67"),sQuery(id+"F28.wireOp",EDGE,"E69"),sQuery(id+"F28.wireOp",EDGE,"E70"),sQuery(id+"F28.wireOp",EDGE,"E71"),sQuery(id+"F28.wireOp",EDGE,"E72"),sQuery(id+"F28.wireOp",EDGE,"E73"),sQuery(id+"F28.wireOp",EDGE,"E74"),sQuery(id+"F28.wireOp",EDGE,"E75"),sQuery(id+"F28.wireOp",EDGE,"E76"),sQuery(id+"F28.wireOp",EDGE,"E77"),sQuery(id+"F28.wireOp",EDGE,"E80"),sQuery(id+"F28.wireOp",EDGE,"E81"),sQuery(id+"F28.wireOp",EDGE,"E82")])]}),"instanceName":"1"});
            transform(context, id + "F45", {"entities" : qUnion([Q0]), "transformType" : TransformType.TRANSLATION_3D, "dx" : 50 * mm, "dy" : 0 * mm, "dz" : 0 * mm, "makeCopy" : false});
        }
    });
